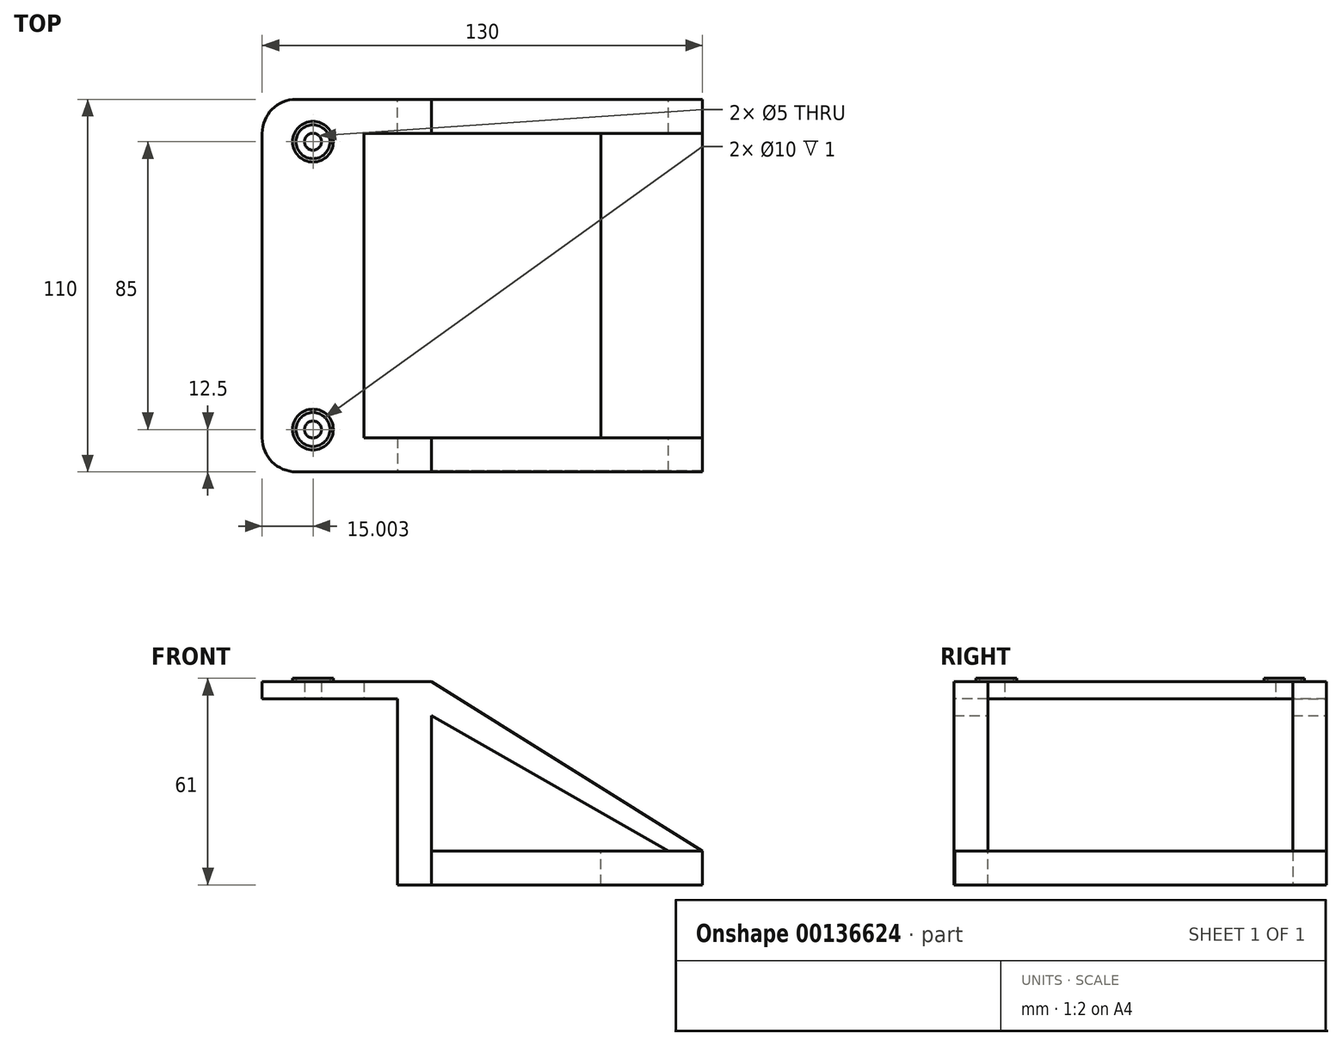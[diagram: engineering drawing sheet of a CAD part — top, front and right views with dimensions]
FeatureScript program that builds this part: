
annotation { "Feature Type Name" : "Feature", "Feature Type Description" : "" }
export const myFeature = defineFeature(function(context is Context, id is Id, definition is map)
    precondition{}
    {
        {
            var Q0;
            Q0=qCreatedBy(makeId("Top.planeOp"),FACE);
            var sketch = newSketch(context, id + "F0", { "sketchPlane" : qUnion([Q0])});
            skLineSegment(sketch, "E0.bottom", {"start": v(-68.02, -108.04) * mm, "end": v(-38.02, -108.04) * mm});
            skLineSegment(sketch, "E0.top", {"start": v(-68.02, 1.96) * mm, "end": v(-38.02, 1.96) * mm});
            skLineSegment(sketch, "E0.left", {"start": v(-68.02, -108.04) * mm, "end": v(-68.02, 1.96) * mm});
            skLineSegment(sketch, "E0.right", {"start": v(-38.02, -108.04) * mm, "end": v(-38.02, 1.96) * mm});
            skPoint(sketch, "E1", {"position": v(-53.02, -10.54) * mm});
            skPoint(sketch, "E1.positionSnap0", {"position": v(-53.02, 1.96) * mm});
            skPoint(sketch, "E2", {"position": v(-53.02, -95.54) * mm});
            skPoint(sketch, "E2.positionSnap0", {"position": v(-53.02, -108.04) * mm});
            skCircle(sketch, "E3", {"center": v(-53.02, -10.54) * mm, "radius": 2.5 * mm});
            skCircle(sketch, "E4", {"center": v(-53.02, -95.54) * mm, "radius": 2.5 * mm});
            skSolve(sketch);
        }
        {
            var Q0;
            Q0=makeQuery(id+"F0.imprint","IMPRINT",FACE,{"disambiguationData":[TD([[makeQuery(id+"F0.imprint","IMPRINT",EDGE,{"derivedFrom":sQuery(id+"F0.wireOp",EDGE,"E0.bottom")}),1.0]])]});
            extrude(context, id + "F1", {"entities" : qUnion([Q0]), "depth" : 5 * mm});
        }
        {
            var Q0;
            Q0=makeQuery(id+"F1.opExtrude","SWEPT_EDGE",EDGE,{"disambiguationData":[OSD([sQuery(id+"F0.wireOp",EDGE,"E0.bottom"),sQuery(id+"F0.wireOp",EDGE,"E0.left")])]});
            var Q1;
            Q1=makeQuery(id+"F1.opExtrude","SWEPT_EDGE",EDGE,{"disambiguationData":[OSD([sQuery(id+"F0.wireOp",EDGE,"E0.top"),sQuery(id+"F0.wireOp",EDGE,"E0.left")])]});
            fillet(context, id + "F2", {"entities" : qUnion([Q0, Q1]), "radius" : 10 * mm, "tangentPropagation" : true, "allowEdgeOverflow" : false});
        }
        {
            var Q0;
            Q0=makeQuery(id+"F1.opExtrude","CAP_FACE",FACE,{"disambiguationData":[OSD([sQuery(id+"F0.wireOp",EDGE,"E0.bottom"),sQuery(id+"F0.wireOp",EDGE,"E0.top"),sQuery(id+"F0.wireOp",EDGE,"E0.left"),sQuery(id+"F0.wireOp",EDGE,"E0.right"),sQuery(id+"F0.wireOp",EDGE,"E3"),sQuery(id+"F0.wireOp",EDGE,"E4")])],"isStart":false});
            var sketch = newSketch(context, id + "F3", { "sketchPlane" : qUnion([Q0])});
            skCircle(sketch, "E5", {"center": v(-53.02, -10.54) * mm, "radius": 5 * mm});
            skCircle(sketch, "E6", {"center": v(-53.02, -95.54) * mm, "radius": 5 * mm});
            skCircle(sketch, "E7", {"center": v(-53.02, -95.54) * mm, "radius": 6 * mm});
            skCircle(sketch, "E8", {"center": v(-53.02, -10.54) * mm, "radius": 6 * mm});
            skSolve(sketch);
        }
        {
            var Q0;
            Q0=makeQuery(id+"F3.imprint","IMPRINT",FACE,{"disambiguationData":[TD([[makeQuery(id+"F3.imprint","IMPRINT",EDGE,{"derivedFrom":sQuery(id+"F3.wireOp",EDGE,"E5")}),-1.0]])]});
            var Q1;
            Q1=makeQuery(id+"F3.imprint","IMPRINT",FACE,{"disambiguationData":[TD([[makeQuery(id+"F3.imprint","IMPRINT",EDGE,{"derivedFrom":sQuery(id+"F3.wireOp",EDGE,"E6")}),-1.0]])]});
            extrude(context, id + "F4", {"entities" : qUnion([Q0, Q1]), "operationType" : NewBodyOperationType.ADD, "depth" : 1 * mm});
        }
        {
            var Q0;
            Q0=makeQuery(id+"F1.opExtrude","SWEPT_FACE",FACE,{"disambiguationData":[OSD([sQuery(id+"F0.wireOp",EDGE,"E0.right")])]});
            var sketch = newSketch(context, id + "F5", { "sketchPlane" : qUnion([Q0])});
            skLineSegment(sketch, "E9.bottom", {"start": v(-108.04, 0) * mm, "end": v(-98.04, 0) * mm});
            skLineSegment(sketch, "E9.top", {"start": v(-108.04, 5) * mm, "end": v(-98.04, 5) * mm});
            skLineSegment(sketch, "E9.left", {"start": v(-108.04, 0) * mm, "end": v(-108.04, 5) * mm});
            skLineSegment(sketch, "E9.right", {"start": v(-98.04, 0) * mm, "end": v(-98.04, 5) * mm});
            skLineSegment(sketch, "E10.bottom", {"start": v(1.96, 5) * mm, "end": v(-8.04, 5) * mm});
            skLineSegment(sketch, "E10.top", {"start": v(1.96, 0) * mm, "end": v(-8.04, 0) * mm});
            skLineSegment(sketch, "E10.left", {"start": v(1.96, 5) * mm, "end": v(1.96, 0) * mm});
            skLineSegment(sketch, "E10.right", {"start": v(-8.04, 5) * mm, "end": v(-8.04, 0) * mm});
            skSolve(sketch);
        }
        {
            var Q0;
            Q0 = qSketchRegion(id + "F5", true);
            extrude(context, id + "F6", {"entities" : qUnion([Q0]), "operationType" : NewBodyOperationType.ADD, "depth" : 20 * mm});
        }
        {
            var Q0;
            Q0=makeQuery(id+"F6.boolean.opBoolean","MERGE",FACE,{"derivedFrom":[makeQuery(id+"F1.opExtrude","CAP_FACE",FACE,{"disambiguationData":[OSD([sQuery(id+"F0.wireOp",EDGE,"E0.bottom"),sQuery(id+"F0.wireOp",EDGE,"E0.top"),sQuery(id+"F0.wireOp",EDGE,"E0.left"),sQuery(id+"F0.wireOp",EDGE,"E0.right"),sQuery(id+"F0.wireOp",EDGE,"E3"),sQuery(id+"F0.wireOp",EDGE,"E4")])],"isStart":true}),makeQuery(id+"F6.opExtrude","SWEPT_FACE",FACE,{"disambiguationData":[OSD([sQuery(id+"F5.wireOp",EDGE,"E9.bottom")])]}),makeQuery(id+"F6.opExtrude","SWEPT_FACE",FACE,{"disambiguationData":[OSD([sQuery(id+"F5.wireOp",EDGE,"E10.top")])]})]});
            var sketch = newSketch(context, id + "F7", { "sketchPlane" : qUnion([Q0])});
            skLineSegment(sketch, "E11.bottom", {"start": v(-28.02, 8.04) * mm, "end": v(-18.02, 8.04) * mm});
            skLineSegment(sketch, "E11.top", {"start": v(-28.02, -1.96) * mm, "end": v(-18.02, -1.96) * mm});
            skLineSegment(sketch, "E11.left", {"start": v(-28.02, 8.04) * mm, "end": v(-28.02, -1.96) * mm});
            skLineSegment(sketch, "E11.right", {"start": v(-18.02, 8.04) * mm, "end": v(-18.02, -1.96) * mm});
            skLineSegment(sketch, "E12.bottom", {"start": v(-28.02, 98.04) * mm, "end": v(-18.02, 98.04) * mm});
            skLineSegment(sketch, "E12.top", {"start": v(-28.02, 108.04) * mm, "end": v(-18.02, 108.04) * mm});
            skLineSegment(sketch, "E12.left", {"start": v(-28.02, 98.04) * mm, "end": v(-28.02, 108.04) * mm});
            skLineSegment(sketch, "E12.right", {"start": v(-18.02, 98.04) * mm, "end": v(-18.02, 108.04) * mm});
            skSolve(sketch);
        }
        {
            var Q0;
            Q0 = qSketchRegion(id + "F7", true);
            extrude(context, id + "F8", {"entities" : qUnion([Q0]), "operationType" : NewBodyOperationType.ADD, "depth" : 55 * mm});
        }
        {
            var Q0;
            Q0=makeQuery(id+"F8.boolean.opBoolean","MERGE",FACE,{"derivedFrom":[makeQuery(id+"F6.opExtrude","CAP_FACE",FACE,{"disambiguationData":[OSD([sQuery(id+"F5.wireOp",EDGE,"E10.bottom"),sQuery(id+"F5.wireOp",EDGE,"E10.top"),sQuery(id+"F5.wireOp",EDGE,"E10.left"),sQuery(id+"F5.wireOp",EDGE,"E10.right")])],"isStart":false}),makeQuery(id+"F8.opExtrude","SWEPT_FACE",FACE,{"disambiguationData":[OSD([sQuery(id+"F7.wireOp",EDGE,"E11.right")])]})]});
            var sketch = newSketch(context, id + "F9", { "sketchPlane" : qUnion([Q0])});
            skLineSegment(sketch, "E13.bottom", {"start": v(-107.85, -55) * mm, "end": v(1.96, -55) * mm});
            skLineSegment(sketch, "E13.top", {"start": v(-107.85, -45) * mm, "end": v(1.96, -45) * mm});
            skLineSegment(sketch, "E13.left", {"start": v(-107.85, -55) * mm, "end": v(-107.85, -45) * mm});
            skLineSegment(sketch, "E13.right", {"start": v(1.96, -55) * mm, "end": v(1.96, -45) * mm});
            skSolve(sketch);
        }
        {
            var Q0;
            Q0 = qSketchRegion(id + "F9", true);
            extrude(context, id + "F10", {"entities" : qUnion([Q0]), "operationType" : NewBodyOperationType.ADD, "depth" : 80 * mm});
        }
        {
            var Q0;
            Q0=makeQuery(id+"F10.opExtrude","CAP_FACE",FACE,{"disambiguationData":[OSD([sQuery(id+"F9.wireOp",EDGE,"E13.bottom"),sQuery(id+"F9.wireOp",EDGE,"E13.top"),sQuery(id+"F9.wireOp",EDGE,"E13.left"),sQuery(id+"F9.wireOp",EDGE,"E13.right")])],"isStart":true});
            extrude(context, id + "F11", {"entities" : qUnion([Q0]), "operationType" : NewBodyOperationType.REMOVE, "oppositeDirection" : true, "depth" : 50 * mm});
        }
        {
            var Q0;
            Q0=makeQuery(id+"F10.boolean.opBoolean","MERGE",FACE,{"derivedFrom":[makeQuery(id+"F8.boolean.opBoolean","MERGE",FACE,{"derivedFrom":[makeQuery(id+"F6.boolean.opBoolean","MERGE",FACE,{"derivedFrom":[makeQuery(id+"F1.opExtrude","SWEPT_FACE",FACE,{"disambiguationData":[OSD([sQuery(id+"F0.wireOp",EDGE,"E0.top")])]}),makeQuery(id+"F6.opExtrude","SWEPT_FACE",FACE,{"disambiguationData":[OSD([sQuery(id+"F5.wireOp",EDGE,"E10.left")])]})]}),makeQuery(id+"F8.opExtrude","SWEPT_FACE",FACE,{"disambiguationData":[OSD([sQuery(id+"F7.wireOp",EDGE,"E11.top")])]})]}),makeQuery(id+"F10.opExtrude","SWEPT_FACE",FACE,{"disambiguationData":[OSD([sQuery(id+"F9.wireOp",EDGE,"E13.right")])]})]});
            var sketch = newSketch(context, id + "F12", { "sketchPlane" : qUnion([Q0])});
            skLineSegment(sketch, "E14", {"start": v(18.02, 5) * mm, "end": v(-61.98, -45) * mm});
            skLineSegment(sketch, "E15", {"start": v(18.02, -5) * mm, "end": v(18.02, 5) * mm});
            skLineSegment(sketch, "E16", {"start": v(18.02, -5) * mm, "end": v(-51.98, -45) * mm});
            skLineSegment(sketch, "E17", {"start": v(-51.98, -45) * mm, "end": v(-61.98, -45) * mm});
            skSolve(sketch);
        }
        {
            var Q0;
            Q0=makeQuery(id+"F12.imprint","IMPRINT",FACE,{"disambiguationData":[TD([[makeQuery(id+"F12.imprint","IMPRINT",EDGE,{"derivedFrom":sQuery(id+"F12.wireOp",EDGE,"E14")}),1.0]])]});
            extrude(context, id + "F13", {"entities" : qUnion([Q0]), "operationType" : NewBodyOperationType.ADD, "oppositeDirection" : true, "depth" : 10 * mm});
        }
        {
            var Q0;
            {var subQ0=sQuery(id+"F7.wireOp",EDGE,"E12.bottom");var subQ1=sQuery(id+"F5.wireOp",EDGE,"E9.right");Q0=makeQuery(id+"F11.boolean.opBoolean","MERGE",FACE,{"derivedFrom":[makeQuery(id+"F8.boolean.opBoolean","MERGE",FACE,{"derivedFrom":[makeQuery(id+"F6.opExtrude","SWEPT_FACE",FACE,{"disambiguationData":[OSD([subQ1])]}),makeQuery(id+"F8.opExtrude","SWEPT_FACE",FACE,{"disambiguationData":[OSD([subQ0])]})]}),makeQuery(id+"F11.opExtrude","SWEPT_FACE",FACE,{"disambiguationData":[OSD([subQ1,subQ0,sQuery(id+"F7.wireOp",EDGE,"E12.right")])]})]});}
            var sketch = newSketch(context, id + "F14", { "sketchPlane" : qUnion([Q0])});
            skLineSegment(sketch, "E18", {"start": v(18.02, 5) * mm, "end": v(-61.93, -45) * mm});
            skPoint(sketch, "E18.endSnap0", {"position": v(-6.98, -45) * mm});
            skLineSegment(sketch, "E19", {"start": v(-61.93, -45) * mm, "end": v(-51.93, -45) * mm});
            skLineSegment(sketch, "E20", {"start": v(-51.93, -45) * mm, "end": v(18.02, -5) * mm});
            skLineSegment(sketch, "E21", {"start": v(18.02, 5) * mm, "end": v(18.02, -5) * mm});
            skSolve(sketch);
        }
        {
            var Q0;
            Q0=makeQuery(id+"F14.imprint","IMPRINT",FACE,{"disambiguationData":[TD([[makeQuery(id+"F14.imprint","IMPRINT",EDGE,{"derivedFrom":sQuery(id+"F14.wireOp",EDGE,"E18")}),1.0]])]});
            extrude(context, id + "F15", {"entities" : qUnion([Q0]), "operationType" : NewBodyOperationType.ADD, "oppositeDirection" : true, "depth" : 10 * mm});
        }
    });
